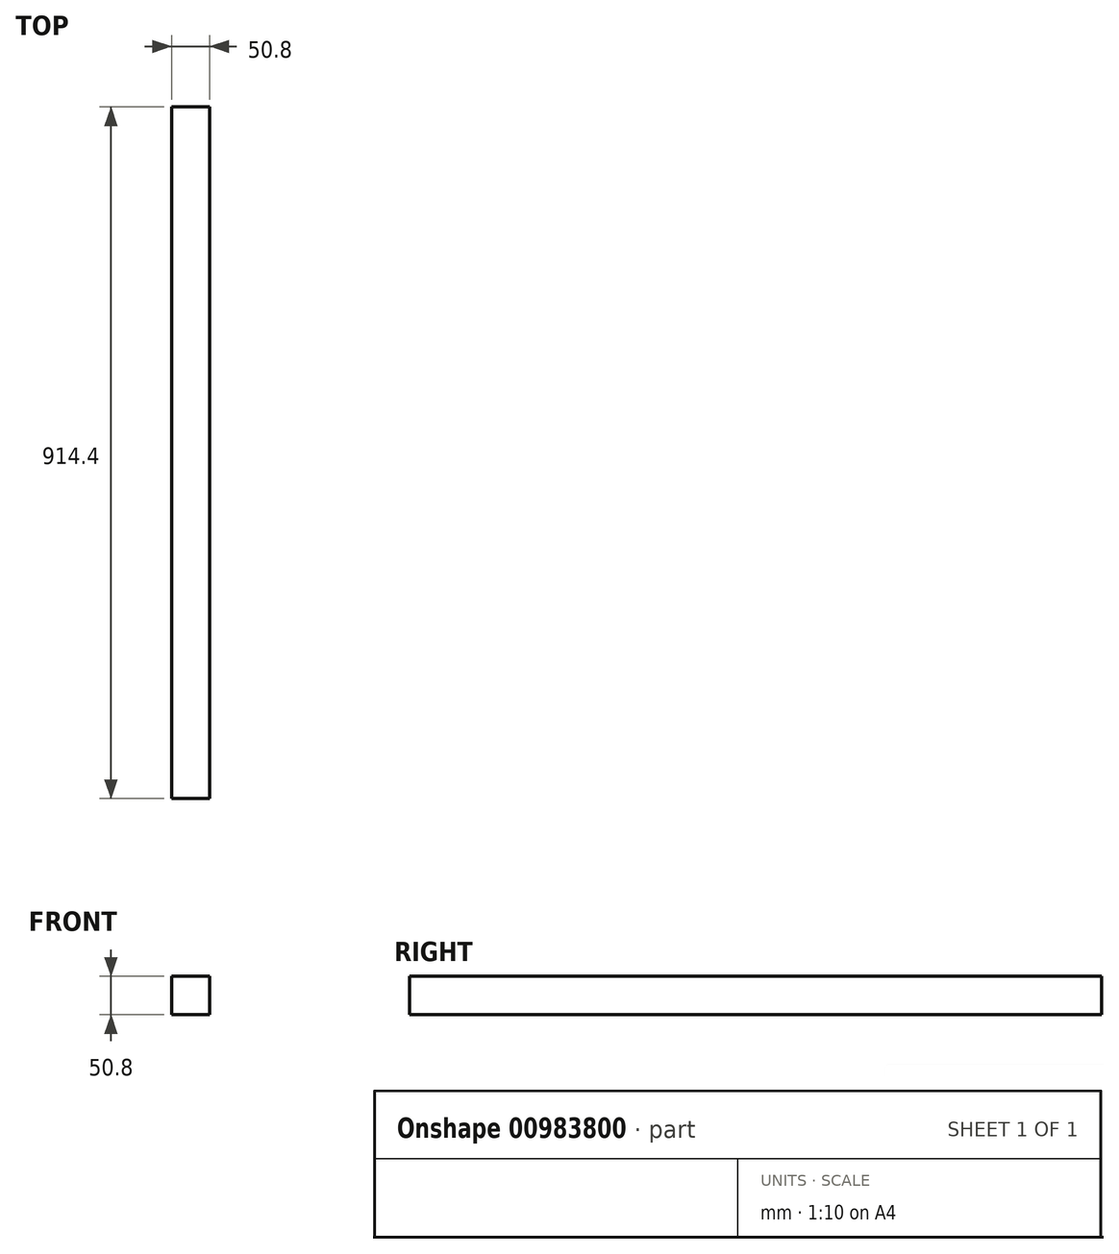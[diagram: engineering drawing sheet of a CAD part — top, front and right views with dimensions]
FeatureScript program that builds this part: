
annotation { "Feature Type Name" : "Feature", "Feature Type Description" : "" }
export const myFeature = defineFeature(function(context is Context, id is Id, definition is map)
    precondition{}
    {
        {
            var Q0;
            Q0=qCreatedBy(makeId("Front.planeOp"),FACE);
            var sketch = newSketch(context, id + "F0", { "sketchPlane" : qUnion([Q0])});
            skLineSegment(sketch, "E0.bottom", {"start": v(25.4, 25.4) * mm, "end": v(-25.4, 25.4) * mm});
            skLineSegment(sketch, "E0.top", {"start": v(25.4, -25.4) * mm, "end": v(-25.4, -25.4) * mm});
            skLineSegment(sketch, "E0.left", {"start": v(25.4, 25.4) * mm, "end": v(25.4, -25.4) * mm});
            skLineSegment(sketch, "E0.right", {"start": v(-25.4, 25.4) * mm, "end": v(-25.4, -25.4) * mm});
            skPoint(sketch, "E0.middle", {"position": v(0, 0) * mm});
            skSolve(sketch);
        }
        {
            var Q0;
            Q0 = qSketchRegion(id + "F0", true);
            extrude(context, id + "F1", {"entities" : qUnion([Q0]), "depth" : 914.4 * mm, "offsetDistance" : 25.4 * mm});
        }
    });
